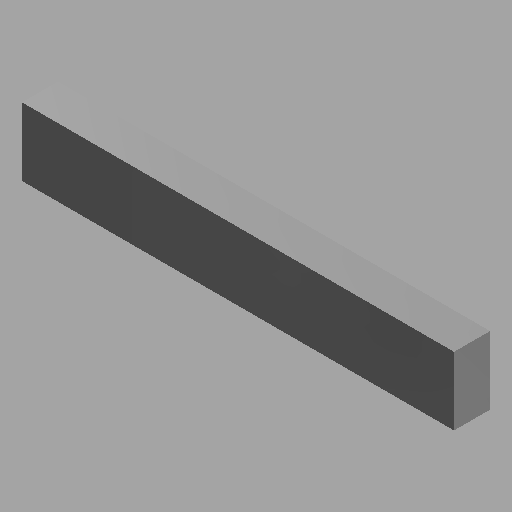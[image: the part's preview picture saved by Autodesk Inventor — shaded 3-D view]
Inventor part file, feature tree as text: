
AUTODESK INVENTOR PART (.ipt)
format: ipt  version: 2023 (Build 270158030, 158C)  size: 95,744 bytes
history: native  units: mm (DEFAULTED — no unit token found)
features: extrude x2, sketch x2
ambient origin geometry x8: Origin, YZ Plane, XZ Plane, XY Plane, X Axis, Y Axis, Z Axis, Center Point
bodies: Solid1 (feature_tree)
feature tree (4):
  extrude  "Extrusion1"  Depth=25.4mm TaperAngle=0.0deg
  extrude  "Extrusion2"  [1 undecoded]
  sketch  "Sketch1"  dims[d0=25.4mm d1=0.0mm d2=25.4mm d3=0.0mm]
  sketch  "Sketch2"
note: 1 required parameter value undecoded (feature->parameter linkage not recoverable at this tier; creation-order binding heuristic only, values carry confidence <= 0.55)
